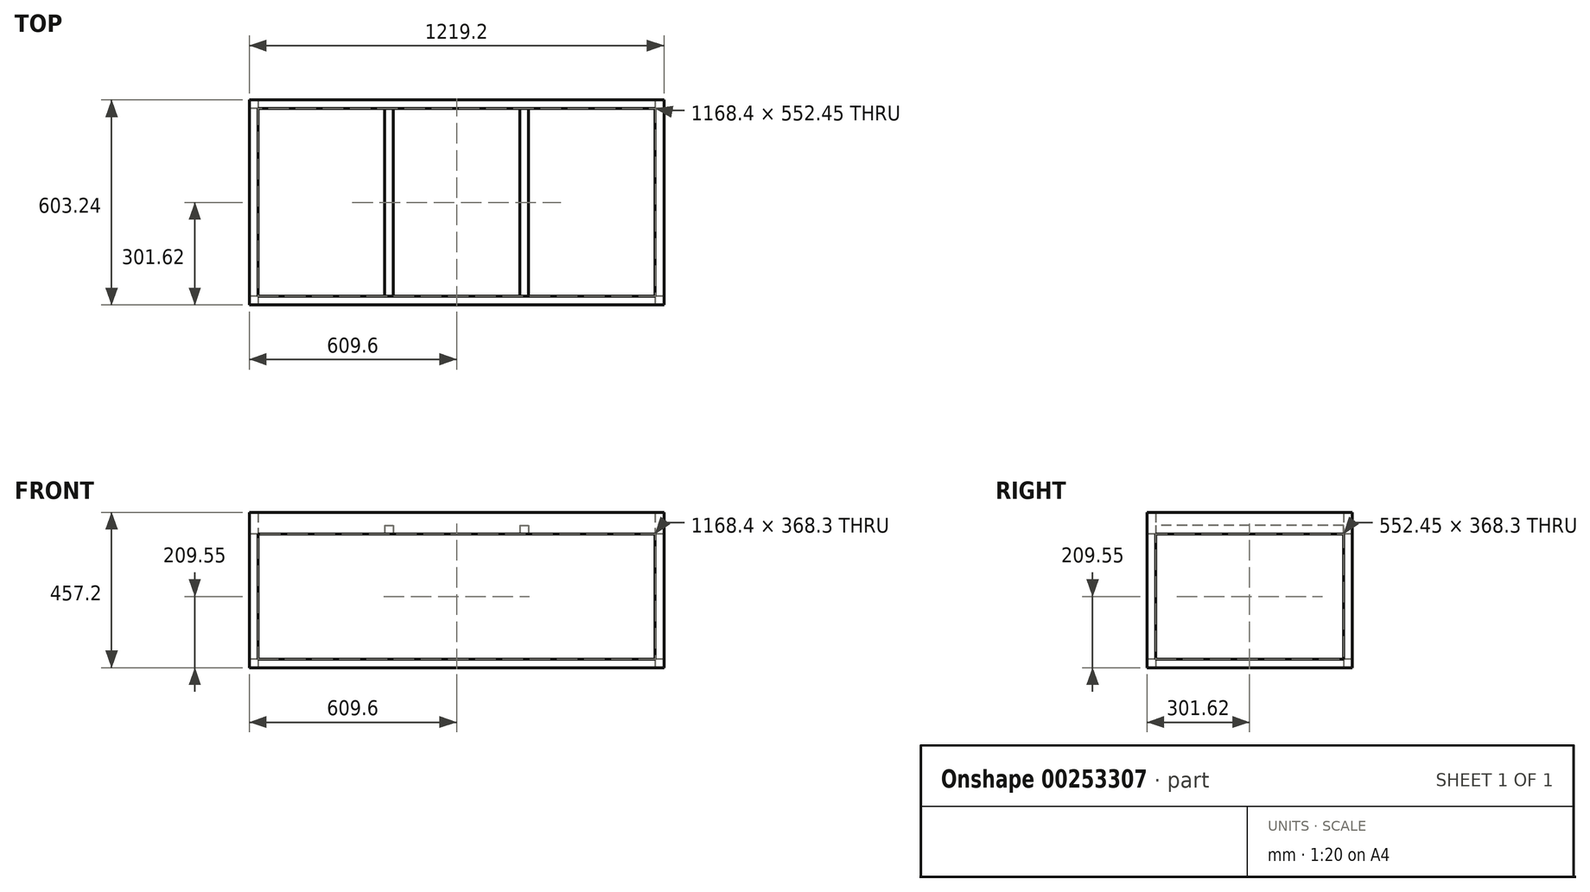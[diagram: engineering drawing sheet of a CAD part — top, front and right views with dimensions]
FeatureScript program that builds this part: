
annotation { "Feature Type Name" : "Feature", "Feature Type Description" : "" }
export const myFeature = defineFeature(function(context is Context, id is Id, definition is map)
    precondition{}
    {
        {
            var Q0;
            Q0=qCreatedBy(makeId("Top.planeOp"),FACE);
            var sketch = newSketch(context, id + "F0", { "sketchPlane" : qUnion([Q0])});
            skLineSegment(sketch, "E0.bottom", {"start": v(609.6, 301.63) * mm, "end": v(-609.6, 301.63) * mm});
            skLineSegment(sketch, "E0.top", {"start": v(609.6, -301.63) * mm, "end": v(-609.6, -301.63) * mm});
            skLineSegment(sketch, "E0.left", {"start": v(609.6, 301.63) * mm, "end": v(609.6, -301.63) * mm});
            skLineSegment(sketch, "E0.right", {"start": v(-609.6, 301.63) * mm, "end": v(-609.6, -301.63) * mm});
            skPoint(sketch, "E0.middle", {"position": v(0, 0) * mm});
            skSolve(sketch);
        }
        {
            var Q0;
            Q0=makeQuery(id+"F0.imprint","IMPRINT",FACE,{"disambiguationData":[TD([[makeQuery(id+"F0.imprint","IMPRINT",EDGE,{"derivedFrom":sQuery(id+"F0.wireOp",EDGE,"E0.bottom")}),1.0]])]});
            extrude(context, id + "F1", {"entities" : qUnion([Q0]), "depth" : 38.1 * mm});
        }
        {
            var Q0;
            Q0=makeQuery(id+"F1.opExtrude","CAP_FACE",FACE,{"disambiguationData":[OSD([sQuery(id+"F0.wireOp",EDGE,"E0.bottom"),sQuery(id+"F0.wireOp",EDGE,"E0.top"),sQuery(id+"F0.wireOp",EDGE,"E0.left"),sQuery(id+"F0.wireOp",EDGE,"E0.right")])],"isStart":true});
            extrude(context, id + "F2", {"entities" : qUnion([Q0]), "depth" : 419.1 * mm});
        }
        {
            var Q0;
            Q0=makeQuery(id+"F2.opExtrude","SWEPT_FACE",FACE,{"disambiguationData":[OSD([sQuery(id+"F0.wireOp",EDGE,"E0.top")])]});
            var sketch = newSketch(context, id + "F3", { "sketchPlane" : qUnion([Q0])});
            skLineSegment(sketch, "E1.bottom", {"start": v(584.2, -25.4) * mm, "end": v(-584.2, -25.4) * mm});
            skLineSegment(sketch, "E1.top", {"start": v(584.2, -393.7) * mm, "end": v(-584.2, -393.7) * mm});
            skLineSegment(sketch, "E1.left", {"start": v(584.2, -25.4) * mm, "end": v(584.2, -393.7) * mm});
            skLineSegment(sketch, "E1.right", {"start": v(-584.2, -25.4) * mm, "end": v(-584.2, -393.7) * mm});
            skPoint(sketch, "E1.middle", {"position": v(0, -209.55) * mm});
            skPoint(sketch, "E1.middle.positionSnap0", {"position": v(609.6, -209.55) * mm});
            skPoint(sketch, "E1.middle.positionSnap1", {"position": v(0, 0) * mm});
            skPoint(sketch, "E1.centerSnap0", {"position": v(609.6, -209.55) * mm});
            skPoint(sketch, "E1.centerSnap1", {"position": v(0, 0) * mm});
            skSolve(sketch);
        }
        {
            var Q0;
            Q0=makeQuery(id+"F3.imprint","IMPRINT",FACE,{"disambiguationData":[TD([[makeQuery(id+"F3.imprint","IMPRINT",EDGE,{"derivedFrom":sQuery(id+"F3.wireOp",EDGE,"E1.bottom")}),1.0]])]});
            extrude(context, id + "F4", {"entities" : qUnion([Q0]), "operationType" : NewBodyOperationType.REMOVE, "endBound" : BoundingType.THROUGH_ALL, "oppositeDirection" : true, "depth" : 25.4 * mm});
        }
        {
            var Q0;
            Q0=makeQuery(id+"F2.opExtrude","SWEPT_FACE",FACE,{"disambiguationData":[OSD([sQuery(id+"F0.wireOp",EDGE,"E0.right")])]});
            var sketch = newSketch(context, id + "F5", { "sketchPlane" : qUnion([Q0])});
            skLineSegment(sketch, "E2.bottom", {"start": v(276.23, -25.4) * mm, "end": v(-276.23, -25.4) * mm});
            skLineSegment(sketch, "E2.top", {"start": v(276.23, -393.7) * mm, "end": v(-276.23, -393.7) * mm});
            skLineSegment(sketch, "E2.left", {"start": v(276.23, -25.4) * mm, "end": v(276.23, -393.7) * mm});
            skLineSegment(sketch, "E2.right", {"start": v(-276.23, -25.4) * mm, "end": v(-276.23, -393.7) * mm});
            skPoint(sketch, "E2.middle", {"position": v(0, -209.55) * mm});
            skPoint(sketch, "E2.middle.positionSnap0", {"position": v(301.63, -209.55) * mm});
            skPoint(sketch, "E2.centerSnap0", {"position": v(301.63, -209.55) * mm});
            skSolve(sketch);
        }
        {
            var Q0;
            Q0=makeQuery(id+"F5.imprint","IMPRINT",FACE,{"disambiguationData":[TD([[makeQuery(id+"F5.imprint","IMPRINT",EDGE,{"derivedFrom":sQuery(id+"F5.wireOp",EDGE,"E2.bottom")}),1.0]])]});
            extrude(context, id + "F6", {"entities" : qUnion([Q0]), "operationType" : NewBodyOperationType.REMOVE, "endBound" : BoundingType.THROUGH_ALL, "oppositeDirection" : true, "depth" : 25.4 * mm});
        }
        {
            var Q0;
            Q0=makeQuery(id+"F2.opExtrude","CAP_FACE",FACE,{"disambiguationData":[OSD([sQuery(id+"F0.wireOp",EDGE,"E0.bottom"),sQuery(id+"F0.wireOp",EDGE,"E0.top"),sQuery(id+"F0.wireOp",EDGE,"E0.left"),sQuery(id+"F0.wireOp",EDGE,"E0.right")])],"isStart":false});
            var sketch = newSketch(context, id + "F7", { "sketchPlane" : qUnion([Q0])});
            skLineSegment(sketch, "E3.bottom", {"start": v(584.2, 276.23) * mm, "end": v(-584.2, 276.23) * mm});
            skLineSegment(sketch, "E3.top", {"start": v(584.2, -276.23) * mm, "end": v(-584.2, -276.23) * mm});
            skLineSegment(sketch, "E3.left", {"start": v(584.2, 276.23) * mm, "end": v(584.2, -276.23) * mm});
            skLineSegment(sketch, "E3.right", {"start": v(-584.2, 276.23) * mm, "end": v(-584.2, -276.23) * mm});
            skPoint(sketch, "E3.middle", {"position": v(0, 0) * mm});
            skSolve(sketch);
        }
        {
            var Q0;
            Q0=makeQuery(id+"F7.imprint","IMPRINT",FACE,{"disambiguationData":[TD([[makeQuery(id+"F7.imprint","IMPRINT",EDGE,{"derivedFrom":sQuery(id+"F7.wireOp",EDGE,"E3.bottom")}),1.0]])]});
            extrude(context, id + "F8", {"entities" : qUnion([Q0]), "operationType" : NewBodyOperationType.REMOVE, "endBound" : BoundingType.THROUGH_ALL, "oppositeDirection" : true, "depth" : 25.4 * mm});
        }
        {
            var Q0;
            {var subQ3=makeQuery(id+"F4.boolean.opBoolean","COPY",FACE,{"derivedFrom":makeQuery(id+"F4.opExtrude","SWEPT_FACE",FACE,{"disambiguationData":[OSD([sQuery(id+"F3.wireOp",EDGE,"E1.bottom")])]})});Q0=makeQuery(id+"F8.boolean.opBoolean","COPY",FACE,{"disambiguationData":[TD([subQ3])],"derivedFrom":makeQuery(id+"F8.opExtrude","SWEPT_FACE",FACE,{"disambiguationData":[OSD([sQuery(id+"F7.wireOp",EDGE,"E3.bottom")])]})});}
            var sketch = newSketch(context, id + "F9", { "sketchPlane" : qUnion([Q0])});
            skLineSegment(sketch, "E4.0", {"start": v(584.2, -25.4) * mm, "end": v(-584.2, -25.4) * mm, "construction": true});
            skLineSegment(sketch, "E4.1", {"start": v(-584.2, 0) * mm, "end": v(-584.2, -25.4) * mm, "construction": true});
            skLineSegment(sketch, "E4.2", {"start": v(584.2, 0) * mm, "end": v(-584.2, 0) * mm, "construction": true});
            skPoint(sketch, "E4.3", {"position": v(584.2, -12.7) * mm});
            skLineSegment(sketch, "E5.bottom", {"start": v(-211.67, 0) * mm, "end": v(-186.27, 0) * mm});
            skLineSegment(sketch, "E5.top", {"start": v(-211.67, -25.4) * mm, "end": v(-186.27, -25.4) * mm});
            skLineSegment(sketch, "E5.left", {"start": v(-211.67, 0) * mm, "end": v(-211.67, -25.4) * mm});
            skLineSegment(sketch, "E5.right", {"start": v(-186.27, 0) * mm, "end": v(-186.27, -25.4) * mm});
            skLineSegment(sketch, "E6.bottom", {"start": v(186.27, 0) * mm, "end": v(211.67, 0) * mm});
            skLineSegment(sketch, "E6.top", {"start": v(186.27, -25.4) * mm, "end": v(211.67, -25.4) * mm});
            skLineSegment(sketch, "E6.left", {"start": v(186.27, 0) * mm, "end": v(186.27, -25.4) * mm});
            skLineSegment(sketch, "E6.right", {"start": v(211.67, 0) * mm, "end": v(211.67, -25.4) * mm});
            skLineSegment(sketch, "E7", {"start": v(-211.67, -12.7) * mm, "end": v(-584.2, -12.7) * mm, "construction": true});
            skLineSegment(sketch, "E8", {"start": v(-186.27, -12.7) * mm, "end": v(186.27, -12.7) * mm, "construction": true});
            skLineSegment(sketch, "E9", {"start": v(211.67, -12.7) * mm, "end": v(584.2, -12.7) * mm, "construction": true});
            skSolve(sketch);
        }
        {
            var Q0;
            Q0 = qSketchRegion(id + "F9", true);
            extrude(context, id + "F10", {"entities" : qUnion([Q0]), "operationType" : NewBodyOperationType.ADD, "endBound" : BoundingType.UP_TO_NEXT, "depth" : 25.4 * mm});
        }
    });
